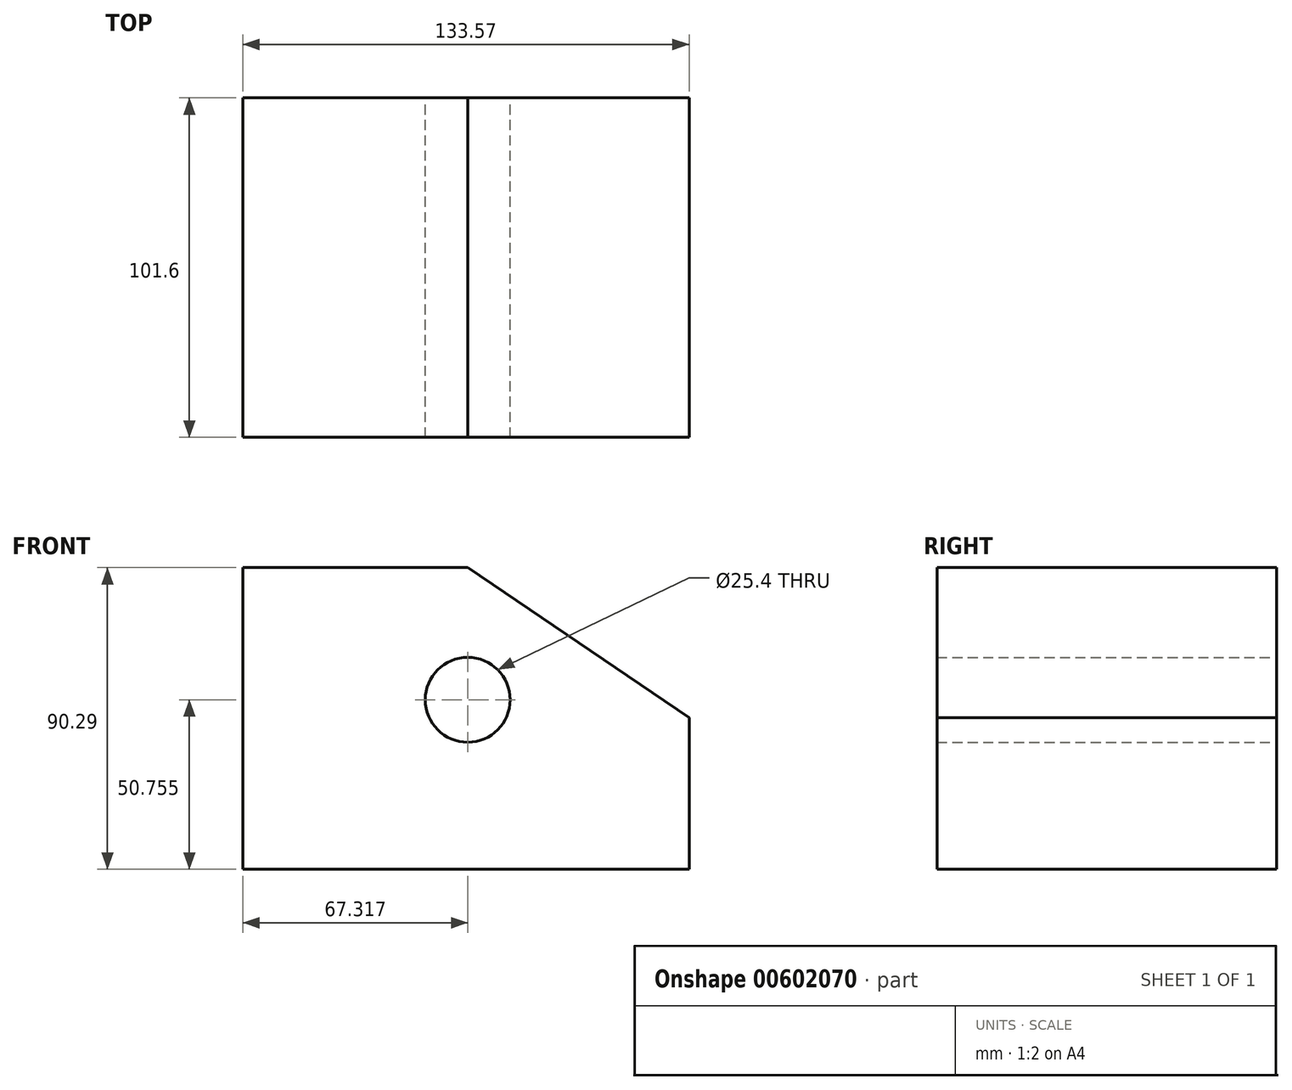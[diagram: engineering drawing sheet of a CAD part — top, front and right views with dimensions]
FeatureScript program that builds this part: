
annotation { "Feature Type Name" : "Feature", "Feature Type Description" : "" }
export const myFeature = defineFeature(function(context is Context, id is Id, definition is map)
    precondition{}
    {
        {
            var Q0;
            Q0=qCreatedBy(makeId("Front.planeOp"),FACE);
            var sketch = newSketch(context, id + "F0", { "sketchPlane" : qUnion([Q0])});
            skLineSegment(sketch, "E0", {"start": v(-112.8, 66.16) * mm, "end": v(-112.8, -24.13) * mm});
            skLineSegment(sketch, "E1", {"start": v(-112.8, -24.13) * mm, "end": v(20.77, -24.13) * mm});
            skLineSegment(sketch, "E2", {"start": v(-112.8, 66.16) * mm, "end": v(-45.48, 66.16) * mm});
            skLineSegment(sketch, "E3", {"start": v(20.77, -24.13) * mm, "end": v(20.77, 21.28) * mm});
            skLineSegment(sketch, "E4", {"start": v(20.77, 21.28) * mm, "end": v(-45.48, 66.16) * mm});
            skPoint(sketch, "E5", {"position": v(-45.48, 26.63) * mm});
            skCircle(sketch, "E6", {"center": v(-45.48, 26.63) * mm, "radius": 12.7 * mm});
            skSolve(sketch);
        }
        {
            var Q0;
            Q0=makeQuery(id+"F0.imprint","IMPRINT",FACE,{"disambiguationData":[TD([[makeQuery(id+"F0.imprint","IMPRINT",EDGE,{"derivedFrom":sQuery(id+"F0.wireOp",EDGE,"E0")}),1.0]])]});
            extrude(context, id + "F1", {"entities" : qUnion([Q0]), "depth" : 101.6 * mm, "offsetDistance" : 25.4 * mm});
        }
    });
